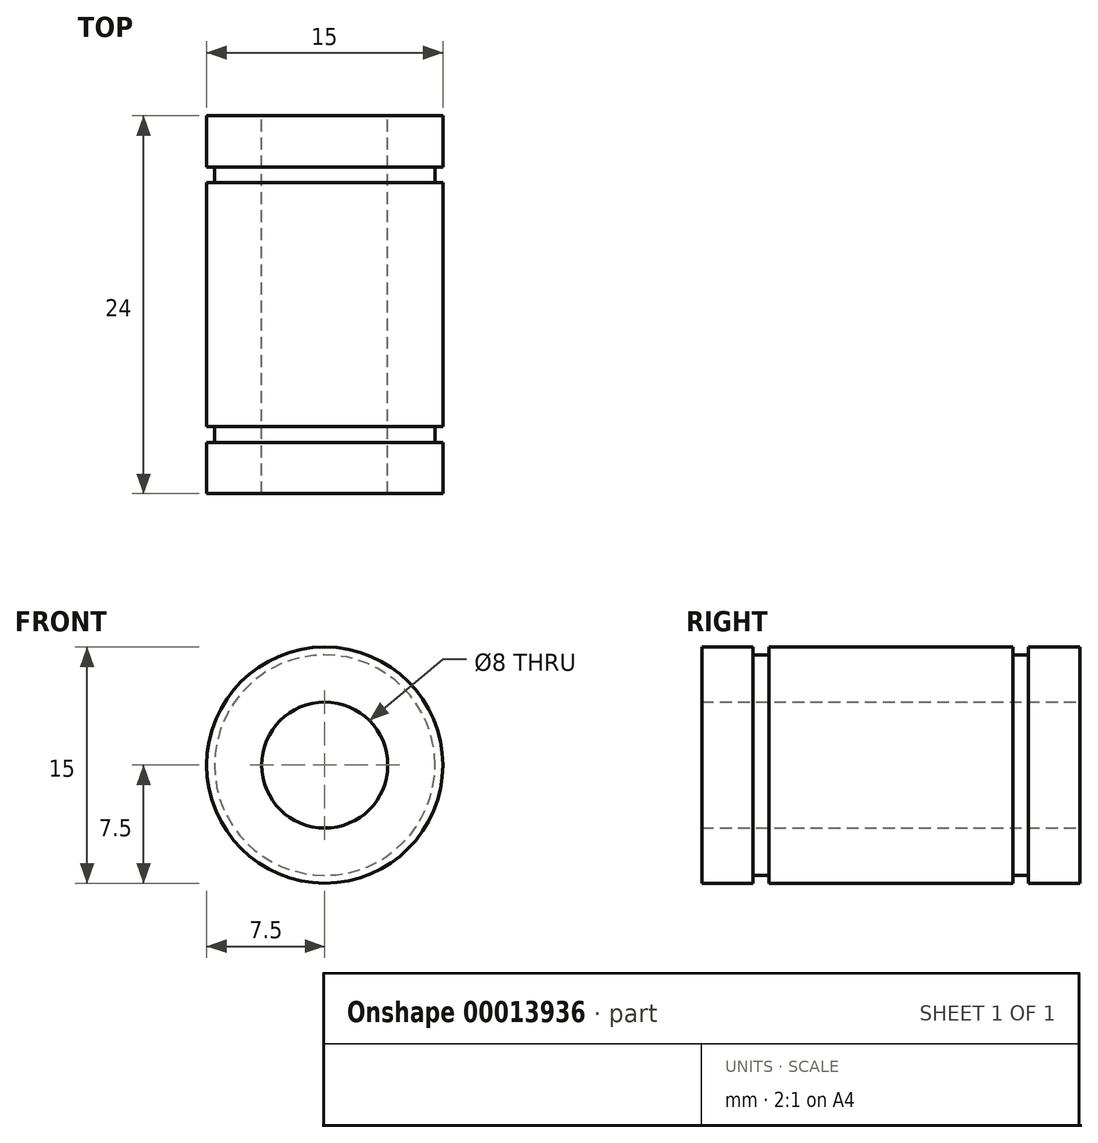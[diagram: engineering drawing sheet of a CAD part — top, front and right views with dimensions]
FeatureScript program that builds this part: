
annotation { "Feature Type Name" : "Feature", "Feature Type Description" : "" }
export const myFeature = defineFeature(function(context is Context, id is Id, definition is map)
    precondition{}
    {
        {
            var Q0;
            Q0=qCreatedBy(makeId("Front.planeOp"),FACE);
            var sketch = newSketch(context, id + "F0", { "sketchPlane" : qUnion([Q0])});
            skCircle(sketch, "E0", {"center": v(0, 0) * mm, "radius": 7.5 * mm});
            skCircle(sketch, "E1", {"center": v(0, 0) * mm, "radius": 4 * mm});
            skSolve(sketch);
        }
        {
            var Q0;
            Q0 = qSketchRegion(id + "F0", true);
            extrude(context, id + "F1", {"entities" : qUnion([Q0]), "depth" : 3.25 * mm});
        }
        {
            var Q0;
            Q0=makeQuery(id+"F1.opExtrude","CAP_FACE",FACE,{"disambiguationData":[OSD([sQuery(id+"F0.wireOp",EDGE,"E0"),sQuery(id+"F0.wireOp",EDGE,"E1")])],"isStart":false});
            var sketch = newSketch(context, id + "F2", { "sketchPlane" : qUnion([Q0])});
            skCircle(sketch, "E2", {"center": v(0, 0) * mm, "radius": 7 * mm});
            skSolve(sketch);
        }
        {
            var Q0;
            Q0=makeQuery(id+"F2.imprint","IMPRINT",FACE,{"disambiguationData":[TD([[makeQuery(id+"F2.imprint","IMPRINT",EDGE,{"derivedFrom":sQuery(id+"F2.wireOp",EDGE,"E2")}),1.0]])]});
            extrude(context, id + "F3", {"entities" : qUnion([Q0]), "operationType" : NewBodyOperationType.ADD, "depth" : 1 * mm});
        }
        {
            var Q0;
            Q0=makeQuery(id+"F3.opExtrude","CAP_FACE",FACE,{"disambiguationData":[OSD([sQuery(id+"F0.wireOp",EDGE,"E1"),sQuery(id+"F2.wireOp",EDGE,"E2")])],"isStart":false});
            var sketch = newSketch(context, id + "F4", { "sketchPlane" : qUnion([Q0])});
            skCircle(sketch, "E3.0", {"center": v(0, 0) * mm, "radius": 7.5 * mm});
            skSolve(sketch);
        }
        {
            var Q0;
            Q0=makeQuery(id+"F4.imprint","IMPRINT",FACE,{"disambiguationData":[TD([[makeQuery(id+"F4.imprint","IMPRINT",EDGE,{"derivedFrom":makeQuery(id+"F3.opExtrude","CAP_EDGE",EDGE,{"disambiguationData":[OSD([sQuery(id+"F2.wireOp",EDGE,"E2")])],"isStart":false})}),1.0]])]});
            var Q1;
            Q1=makeQuery(id+"F4.imprint","IMPRINT",FACE,{"disambiguationData":[TD([[makeQuery(id+"F4.imprint","IMPRINT",EDGE,{"derivedFrom":sQuery(id+"F4.wireOp",EDGE,"E3.0")}),1.0]])]});
            extrude(context, id + "F5", {"entities" : qUnion([Q0, Q1]), "operationType" : NewBodyOperationType.ADD, "depth" : 15.5 * mm});
        }
        {
            var Q0;
            Q0=makeQuery(id+"F5.opExtrude","CAP_FACE",FACE,{"disambiguationData":[OSD([sQuery(id+"F0.wireOp",EDGE,"E1"),sQuery(id+"F4.wireOp",EDGE,"E3.0")])],"isStart":false});
            var sketch = newSketch(context, id + "F6", { "sketchPlane" : qUnion([Q0])});
            skCircle(sketch, "E4.0", {"center": v(0, 0) * mm, "radius": 7 * mm});
            skSolve(sketch);
        }
        {
            var Q0;
            Q0=makeQuery(id+"F6.imprint","IMPRINT",FACE,{"disambiguationData":[TD([[makeQuery(id+"F6.imprint","IMPRINT",EDGE,{"derivedFrom":sQuery(id+"F6.wireOp",EDGE,"E4.0")}),1.0]])]});
            extrude(context, id + "F7", {"entities" : qUnion([Q0]), "operationType" : NewBodyOperationType.ADD, "depth" : 1 * mm});
        }
        {
            var Q0;
            Q0=makeQuery(id+"F7.opExtrude","CAP_FACE",FACE,{"disambiguationData":[OSD([sQuery(id+"F0.wireOp",EDGE,"E1"),sQuery(id+"F6.wireOp",EDGE,"E4.0")])],"isStart":false});
            var sketch = newSketch(context, id + "F8", { "sketchPlane" : qUnion([Q0])});
            skCircle(sketch, "E5.0", {"center": v(0, 0) * mm, "radius": 7.5 * mm});
            skSolve(sketch);
        }
        {
            var Q0;
            Q0=makeQuery(id+"F8.imprint","IMPRINT",FACE,{"disambiguationData":[TD([[makeQuery(id+"F8.imprint","IMPRINT",EDGE,{"derivedFrom":sQuery(id+"F8.wireOp",EDGE,"E5.0")}),1.0]])]});
            var Q1;
            Q1=makeQuery(id+"F8.imprint","IMPRINT",FACE,{"disambiguationData":[TD([[makeQuery(id+"F8.imprint","IMPRINT",EDGE,{"derivedFrom":makeQuery(id+"F7.opExtrude","CAP_EDGE",EDGE,{"disambiguationData":[OSD([sQuery(id+"F6.wireOp",EDGE,"E4.0")])],"isStart":false})}),1.0]])]});
            extrude(context, id + "F9", {"entities" : qUnion([Q0, Q1]), "operationType" : NewBodyOperationType.ADD, "depth" : 3.25 * mm});
        }
    });
